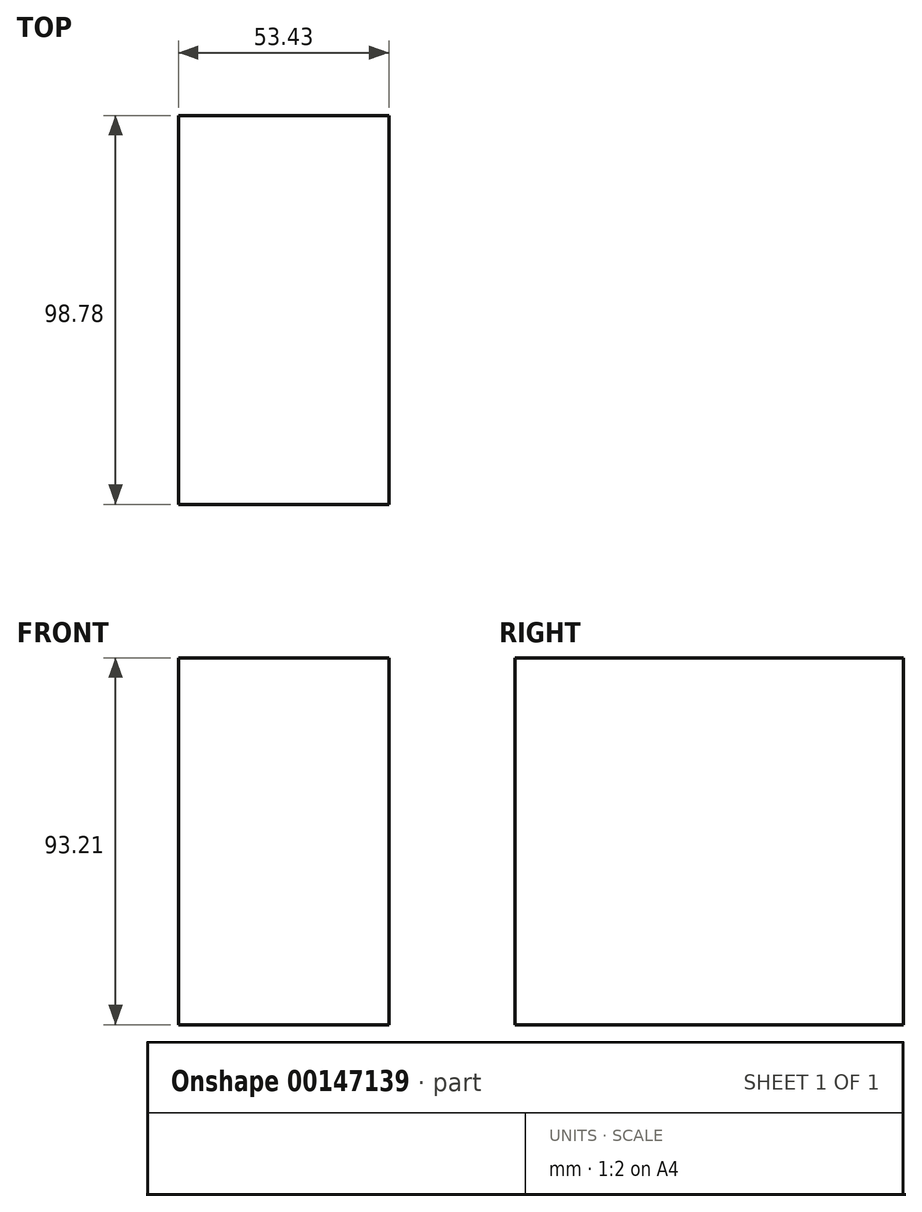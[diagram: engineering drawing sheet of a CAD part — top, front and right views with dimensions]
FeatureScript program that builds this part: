
annotation { "Feature Type Name" : "Feature", "Feature Type Description" : "" }
export const myFeature = defineFeature(function(context is Context, id is Id, definition is map)
    precondition{}
    {
        {
            var Q0;
            Q0=qCreatedBy(makeId("Front.planeOp"),FACE);
            var sketch = newSketch(context, id + "F1", { "sketchPlane" : qUnion([Q0])});
            skLineSegment(sketch, "E0.bottom", {"start": v(53.43, 93.21) * mm, "end": v(0, 93.21) * mm});
            skLineSegment(sketch, "E0.top", {"start": v(53.43, 0) * mm, "end": v(0, 0) * mm});
            skLineSegment(sketch, "E0.left", {"start": v(53.43, 93.21) * mm, "end": v(53.43, 0) * mm});
            skLineSegment(sketch, "E0.right", {"start": v(0, 93.21) * mm, "end": v(0, 0) * mm});
            skSolve(sketch);
        }
        {
            var Q0;
            Q0=makeQuery(id+"F1.imprint","IMPRINT",FACE,{"disambiguationData":[TD([[makeQuery(id+"F1.imprint","IMPRINT",EDGE,{"derivedFrom":sQuery(id+"F1.wireOp",EDGE,"E0.bottom")}),1.0]])]});
            extrude(context, id + "F0", {"entities" : qUnion([Q0]), "depth" : 98.78 * mm});
        }
    });
